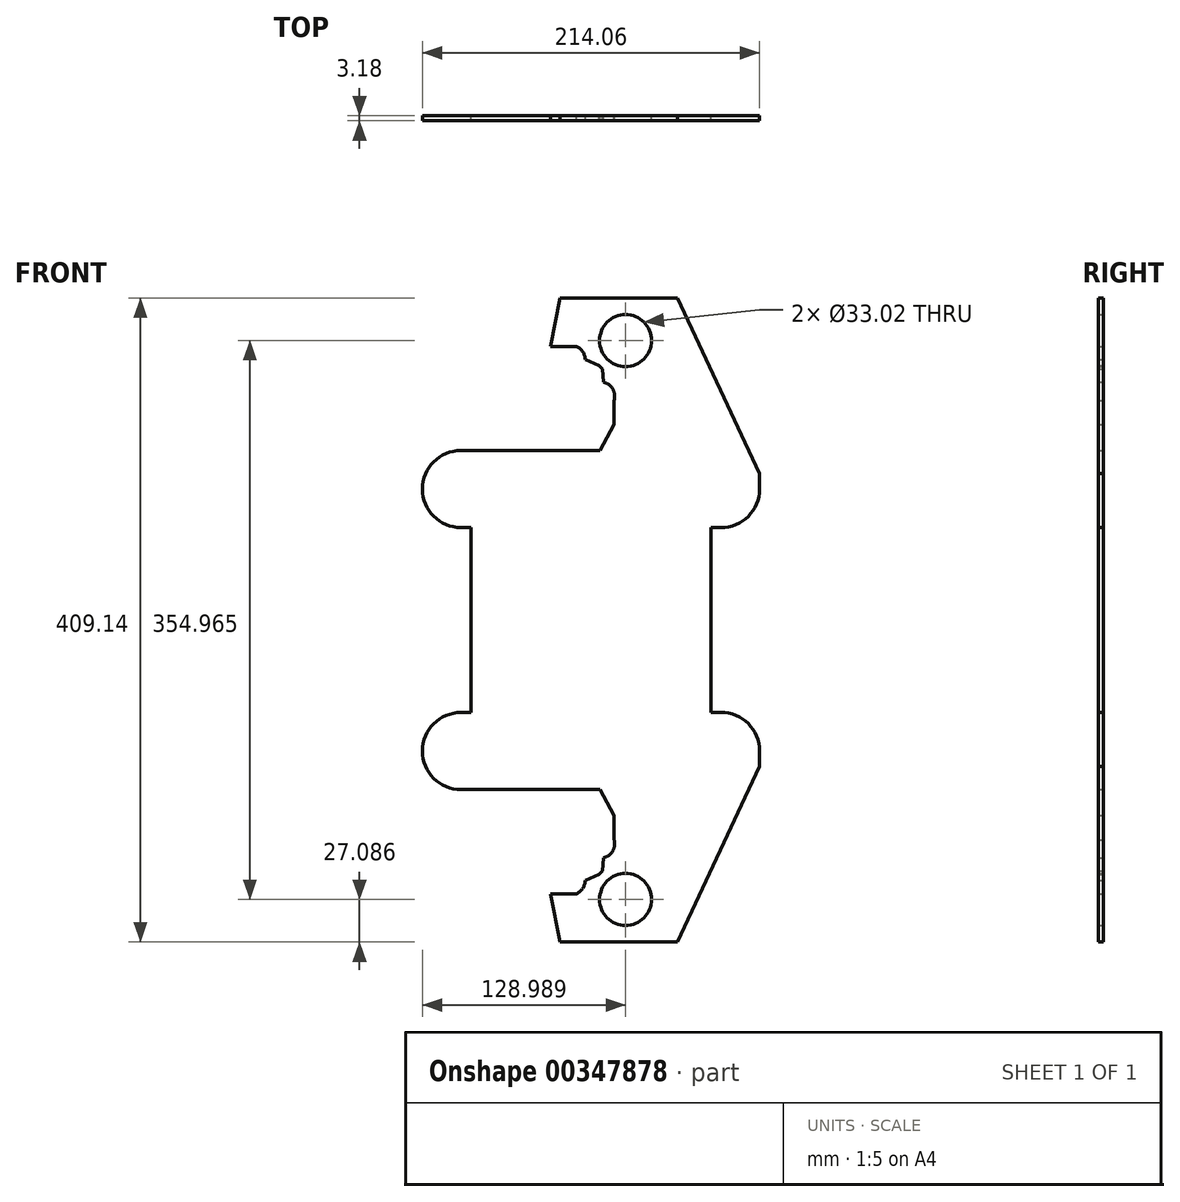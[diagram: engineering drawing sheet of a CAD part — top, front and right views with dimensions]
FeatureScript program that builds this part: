
annotation { "Feature Type Name" : "Feature", "Feature Type Description" : "" }
export const myFeature = defineFeature(function(context is Context, id is Id, definition is map)
    precondition{}
    {
        {
            var Q0;
            Q0=qCreatedBy(makeId("Front.planeOp"),FACE);
            var sketch = newSketch(context, id + "F0", { "sketchPlane" : qUnion([Q0])});
            skLineSegment(sketch, "E0", {"start": v(-4.64, -19.28) * mm, "end": v(-4.64, -15.53) * mm, "construction": true});
            skPoint(sketch, "E1", {"position": v(72.17, -39.98) * mm});
            skArc(sketch, "E2", {"start": v(72.17, -64.5) * mm, "mid": v(89.5, -57.32) * mm, "end": v(96.68, -39.98) * mm});
            skLineSegment(sketch, "E3", {"start": v(-19.49, 50.67) * mm, "end": v(-36, 50.68) * mm});
            skArc(sketch, "E4", {"start": v(-13.97, 42.17) * mm, "mid": v(-15.58, 47.16) * mm, "end": v(-19.49, 50.67) * mm});
            skLineSegment(sketch, "E5", {"start": v(-2.36, 27.9) * mm, "end": v(-2.9, 36.1) * mm});
            skLineSegment(sketch, "E6", {"start": v(-2.9, 36.1) * mm, "end": v(-5.4, 38.35) * mm});
            skLineSegment(sketch, "E7", {"start": v(-5.4, 38.35) * mm, "end": v(-13.97, 42.17) * mm});
            skCircle(sketch, "E8", {"center": v(11.6, 54.31) * mm, "radius": 16.51 * mm});
            skLineSegment(sketch, "E9", {"start": v(4.29, 1.01) * mm, "end": v(-4.64, -15.53) * mm});
            skLineSegment(sketch, "E10", {"start": v(-29.95, 81.4) * mm, "end": v(-36, 50.68) * mm});
            skLineSegment(sketch, "E11", {"start": v(96.68, -39.98) * mm, "end": v(96.68, -30.06) * mm});
            skPoint(sketch, "E12", {"position": v(-4.64, 18.83) * mm});
            skArc(sketch, "E13", {"start": v(-2.36, 27.9) * mm, "mid": v(3.44, 23.54) * mm, "end": v(4.37, 16.35) * mm});
            skLineSegment(sketch, "E14", {"start": v(4.29, 16.25) * mm, "end": v(4.37, 16.35) * mm});
            skLineSegment(sketch, "E15", {"start": v(-29.95, 81.4) * mm, "end": v(44.47, 81.4) * mm});
            skLineSegment(sketch, "E16", {"start": v(33.12, 53.5) * mm, "end": v(39.47, 53.5) * mm});
            skLineSegment(sketch, "E17", {"start": v(36.3, 56.67) * mm, "end": v(36.3, 50.32) * mm});
            skPoint(sketch, "E18", {"position": v(36.3, 53.5) * mm});
            skLineSegment(sketch, "E19", {"start": v(-16.53, 53.53) * mm, "end": v(-10.18, 53.53) * mm});
            skLineSegment(sketch, "E20", {"start": v(-13.35, 56.7) * mm, "end": v(-13.35, 50.36) * mm});
            skPoint(sketch, "E21", {"position": v(-13.35, 53.53) * mm});
            skLineSegment(sketch, "E22", {"start": v(8.36, 14.4) * mm, "end": v(14.7, 14.4) * mm});
            skLineSegment(sketch, "E23", {"start": v(11.53, 17.58) * mm, "end": v(11.53, 11.23) * mm});
            skPoint(sketch, "E24", {"position": v(11.53, 14.4) * mm});
            skPoint(sketch, "E25", {"position": v(-4.64, -22.46) * mm});
            skPoint(sketch, "E26", {"position": v(-4.64, -57.5) * mm});
            skLineSegment(sketch, "E27", {"start": v(72.17, -64.5) * mm, "end": v(72.17, -15.53) * mm, "construction": true});
            skLineSegment(sketch, "E28", {"start": v(72.17, -15.53) * mm, "end": v(-4.64, -15.53) * mm, "construction": true});
            skLineSegment(sketch, "E29", {"start": v(4.29, 1.01) * mm, "end": v(4.37, 16.35) * mm});
            skLineSegment(sketch, "E30", {"start": v(-92.93, -64.44) * mm, "end": v(-92.93, -15.53) * mm, "construction": true});
            skLineSegment(sketch, "E31", {"start": v(-92.93, -15.53) * mm, "end": v(-4.64, -15.53) * mm});
            skLineSegment(sketch, "E32", {"start": v(-96.1, -39.98) * mm, "end": v(-89.75, -39.98) * mm});
            skLineSegment(sketch, "E33", {"start": v(-92.93, -36.8) * mm, "end": v(-92.93, -43.16) * mm});
            skPoint(sketch, "E34", {"position": v(-92.93, -39.98) * mm});
            skLineSegment(sketch, "E35", {"start": v(69, -39.98) * mm, "end": v(75.35, -39.98) * mm});
            skLineSegment(sketch, "E36", {"start": v(72.17, -36.8) * mm, "end": v(72.17, -43.16) * mm});
            skLineSegment(sketch, "E37", {"start": v(-7.82, -57.5) * mm, "end": v(-1.47, -57.5) * mm});
            skLineSegment(sketch, "E38", {"start": v(-4.64, -54.33) * mm, "end": v(-4.64, -60.68) * mm});
            skLineSegment(sketch, "E39", {"start": v(-7.82, -22.46) * mm, "end": v(-1.47, -22.46) * mm});
            skLineSegment(sketch, "E40", {"start": v(-4.64, -19.28) * mm, "end": v(-4.64, -25.63) * mm});
            skLineSegment(sketch, "E41", {"start": v(44.47, 81.4) * mm, "end": v(96.68, -30.06) * mm});
            skLineSegment(sketch, "E42", {"start": v(-92.93, -39.98) * mm, "end": v(72.17, -39.98) * mm, "construction": true});
            skLineSegment(sketch, "E43", {"start": v(-117.44, -40.04) * mm, "end": v(96.68, -39.98) * mm, "construction": true});
            skLineSegment(sketch, "E44", {"start": v(59.47, -64.38) * mm, "end": v(60.14, 11.81) * mm, "construction": true});
            skLineSegment(sketch, "E45", {"start": v(56.96, 11.81) * mm, "end": v(63.31, 11.81) * mm});
            skLineSegment(sketch, "E46", {"start": v(60.14, 14.99) * mm, "end": v(60.14, 8.64) * mm});
            skPoint(sketch, "E47", {"position": v(60.14, 11.81) * mm});
            skLineSegment(sketch, "E48", {"start": v(-92.93, -64.44) * mm, "end": v(-86.58, -64.44) * mm});
            skLineSegment(sketch, "E49", {"start": v(-86.58, -64.44) * mm, "end": v(-11.27, -63.76) * mm, "construction": true});
            skLineSegment(sketch, "E50", {"start": v(-86.58, -64.44) * mm, "end": v(-86.58, -77.73) * mm});
            skLineSegment(sketch, "E51", {"start": v(-86.58, -77.73) * mm, "end": v(-86.58, -168.61) * mm});
            skLineSegment(sketch, "E52", {"start": v(72.17, -64.5) * mm, "end": v(65.84, -64.44) * mm});
            skLineSegment(sketch, "E53", {"start": v(65.84, -168.61) * mm, "end": v(-86.58, -168.61) * mm});
            skLineSegment(sketch, "E54", {"start": v(-86.58, -77.73) * mm, "end": v(65.84, -77.73) * mm});
            skLineSegment(sketch, "E55", {"start": v(65.84, -64.44) * mm, "end": v(65.84, -77.73) * mm});
            skLineSegment(sketch, "E56", {"start": v(65.84, -168.61) * mm, "end": v(65.84, -77.73) * mm});
            skArc(sketch, "E57", {"start": v(-92.93, -15.53) * mm, "mid": v(-117.38, -39.98) * mm, "end": v(-92.93, -64.44) * mm});
            skLineSegment(sketch, "E58", {"start": v(-11.27, -63.76) * mm, "end": v(65.84, -64.44) * mm, "construction": true});
            skLineSegment(sketch, "E59", {"start": v(-86.58, -123.17) * mm, "end": v(65.84, -123.17) * mm, "construction": true});
            skLineSegment(sketch, "E60.MirrorCS", {"start": v(-4.64, -227.06) * mm, "end": v(-4.64, -220.71) * mm});
            skLineSegment(sketch, "E61.MirrorCS", {"start": v(-4.64, -227.06) * mm, "end": v(-4.64, -230.82) * mm, "construction": true});
            skLineSegment(sketch, "E62.MirrorCS", {"start": v(4.29, -247.36) * mm, "end": v(-4.64, -230.82) * mm});
            skLineSegment(sketch, "E63.MirrorCS", {"start": v(-7.82, -223.89) * mm, "end": v(-1.47, -223.89) * mm});
            skLineSegment(sketch, "E64.MirrorCS", {"start": v(11.53, -263.92) * mm, "end": v(11.53, -257.57) * mm});
            skLineSegment(sketch, "E65.MirrorCS", {"start": v(4.29, -262.6) * mm, "end": v(4.37, -262.7) * mm});
            skLineSegment(sketch, "E66.MirrorCS", {"start": v(-7.82, -188.83) * mm, "end": v(-1.47, -188.83) * mm});
            skLineSegment(sketch, "E67.MirrorCS", {"start": v(-4.64, -192) * mm, "end": v(-4.64, -185.66) * mm});
            skLineSegment(sketch, "E68.MirrorCS", {"start": v(-92.93, -181.9) * mm, "end": v(-86.58, -181.9) * mm});
            skLineSegment(sketch, "E69.MirrorCS", {"start": v(69, -206.36) * mm, "end": v(75.35, -206.36) * mm});
            skLineSegment(sketch, "E70.MirrorCS", {"start": v(4.29, -247.36) * mm, "end": v(4.37, -262.7) * mm});
            skLineSegment(sketch, "E71.MirrorCS", {"start": v(8.36, -260.75) * mm, "end": v(14.7, -260.75) * mm});
            skLineSegment(sketch, "E72.MirrorCS", {"start": v(72.17, -209.54) * mm, "end": v(72.17, -203.19) * mm});
            skLineSegment(sketch, "E73.MirrorCS", {"start": v(-2.9, -282.45) * mm, "end": v(-5.4, -284.7) * mm});
            skLineSegment(sketch, "E74.MirrorCS", {"start": v(72.17, -181.85) * mm, "end": v(65.84, -181.9) * mm});
            skLineSegment(sketch, "E75.MirrorCS", {"start": v(-92.93, -209.54) * mm, "end": v(-92.93, -203.19) * mm});
            skArc(sketch, "E76.MirrorCS", {"start": v(-13.97, -288.5) * mm, "mid": v(-15.58, -293.5) * mm, "end": v(-19.49, -297.02) * mm});
            skLineSegment(sketch, "E77.MirrorCS", {"start": v(-2.36, -274.24) * mm, "end": v(-2.9, -282.45) * mm});
            skLineSegment(sketch, "E78.MirrorCS", {"start": v(-5.4, -284.7) * mm, "end": v(-13.97, -288.5) * mm});
            skArc(sketch, "E79.MirrorCS", {"start": v(-2.36, -274.24) * mm, "mid": v(3.44, -269.89) * mm, "end": v(4.37, -262.7) * mm});
            skLineSegment(sketch, "E80.MirrorCS", {"start": v(-96.1, -206.36) * mm, "end": v(-89.75, -206.36) * mm});
            skLineSegment(sketch, "E81.MirrorCS", {"start": v(33.12, -299.84) * mm, "end": v(39.47, -299.84) * mm});
            skLineSegment(sketch, "E82.MirrorCS", {"start": v(-16.53, -299.87) * mm, "end": v(-10.18, -299.87) * mm});
            skLineSegment(sketch, "E83.MirrorCS", {"start": v(56.96, -258.16) * mm, "end": v(63.31, -258.16) * mm});
            skLineSegment(sketch, "E84.MirrorCS", {"start": v(-13.35, -303.05) * mm, "end": v(-13.35, -296.7) * mm});
            skLineSegment(sketch, "E85.MirrorCS", {"start": v(60.14, -261.33) * mm, "end": v(60.14, -254.98) * mm});
            skPoint(sketch, "E86.MirrorP", {"position": v(-4.64, -188.83) * mm});
            skLineSegment(sketch, "E87.MirrorCS", {"start": v(36.3, -303.02) * mm, "end": v(36.3, -296.67) * mm});
            skArc(sketch, "E88.MirrorCS", {"start": v(72.17, -181.85) * mm, "mid": v(89.5, -189.03) * mm, "end": v(96.68, -206.36) * mm});
            skLineSegment(sketch, "E89.MirrorCS", {"start": v(-19.49, -297.02) * mm, "end": v(-36, -297.03) * mm});
            skCircle(sketch, "E90.MirrorC", {"center": v(11.6, -300.65) * mm, "radius": 16.51 * mm});
            skLineSegment(sketch, "E91.MirrorCS", {"start": v(96.68, -206.36) * mm, "end": v(96.68, -216.29) * mm});
            skPoint(sketch, "E92.MirrorP", {"position": v(-4.64, -223.89) * mm});
            skLineSegment(sketch, "E93.MirrorCS", {"start": v(72.17, -181.85) * mm, "end": v(72.17, -230.82) * mm, "construction": true});
            skLineSegment(sketch, "E94.MirrorCS", {"start": v(59.47, -181.96) * mm, "end": v(60.14, -258.16) * mm, "construction": true});
            skLineSegment(sketch, "E95.MirrorCS", {"start": v(-92.93, -181.9) * mm, "end": v(-92.93, -230.82) * mm, "construction": true});
            skLineSegment(sketch, "E96.MirrorCS", {"start": v(-29.95, -327.74) * mm, "end": v(44.47, -327.74) * mm});
            skLineSegment(sketch, "E97.MirrorCS", {"start": v(-29.95, -327.74) * mm, "end": v(-36, -297.03) * mm});
            skPoint(sketch, "E98.MirrorP", {"position": v(36.3, -299.84) * mm});
            skLineSegment(sketch, "E99.MirrorCS", {"start": v(-117.44, -206.3) * mm, "end": v(96.68, -206.36) * mm, "construction": true});
            skPoint(sketch, "E100.MirrorP", {"position": v(60.14, -258.16) * mm});
            skPoint(sketch, "E101.MirrorP", {"position": v(-13.35, -299.87) * mm});
            skArc(sketch, "E102.MirrorCS", {"start": v(-92.93, -230.82) * mm, "mid": v(-117.38, -206.36) * mm, "end": v(-92.93, -181.9) * mm});
            skLineSegment(sketch, "E103.MirrorCS", {"start": v(72.17, -230.82) * mm, "end": v(-4.64, -230.82) * mm, "construction": true});
            skPoint(sketch, "E104.MirrorP", {"position": v(11.53, -260.75) * mm});
            skLineSegment(sketch, "E105.MirrorCS", {"start": v(-92.93, -206.36) * mm, "end": v(72.17, -206.36) * mm, "construction": true});
            skLineSegment(sketch, "E106.MirrorCS", {"start": v(-11.27, -182.58) * mm, "end": v(65.84, -181.9) * mm, "construction": true});
            skLineSegment(sketch, "E107.MirrorCS", {"start": v(44.47, -327.74) * mm, "end": v(96.68, -216.29) * mm});
            skLineSegment(sketch, "E108.MirrorCS", {"start": v(-92.93, -230.82) * mm, "end": v(-4.64, -230.82) * mm});
            skLineSegment(sketch, "E109.MirrorCS", {"start": v(-86.58, -181.9) * mm, "end": v(-11.27, -182.58) * mm, "construction": true});
            skLineSegment(sketch, "E110", {"start": v(65.84, -181.9) * mm, "end": v(65.84, -168.61) * mm});
            skLineSegment(sketch, "E111", {"start": v(-86.58, -181.9) * mm, "end": v(-86.58, -168.61) * mm});
            skSolve(sketch);
        }
        {
            var Q0;
            Q0=makeQuery(id+"F0.imprint","IMPRINT",FACE,{"disambiguationData":[TD([[makeQuery(id+"F0.imprint","IMPRINT",EDGE,{"derivedFrom":sQuery(id+"F0.wireOp",EDGE,"hgDJoyhs-avOh-k2XS-gEzC-Oh4LszvJW2BN")}),-1.0]])]});
            var Q1;
            Q1=qSketchRegion(id+"F0",true);
            extrude(context, id + "F1", {"entities" : qUnion([Q0, Q1]), "depth" : 3.17 * mm});
        }
    });
